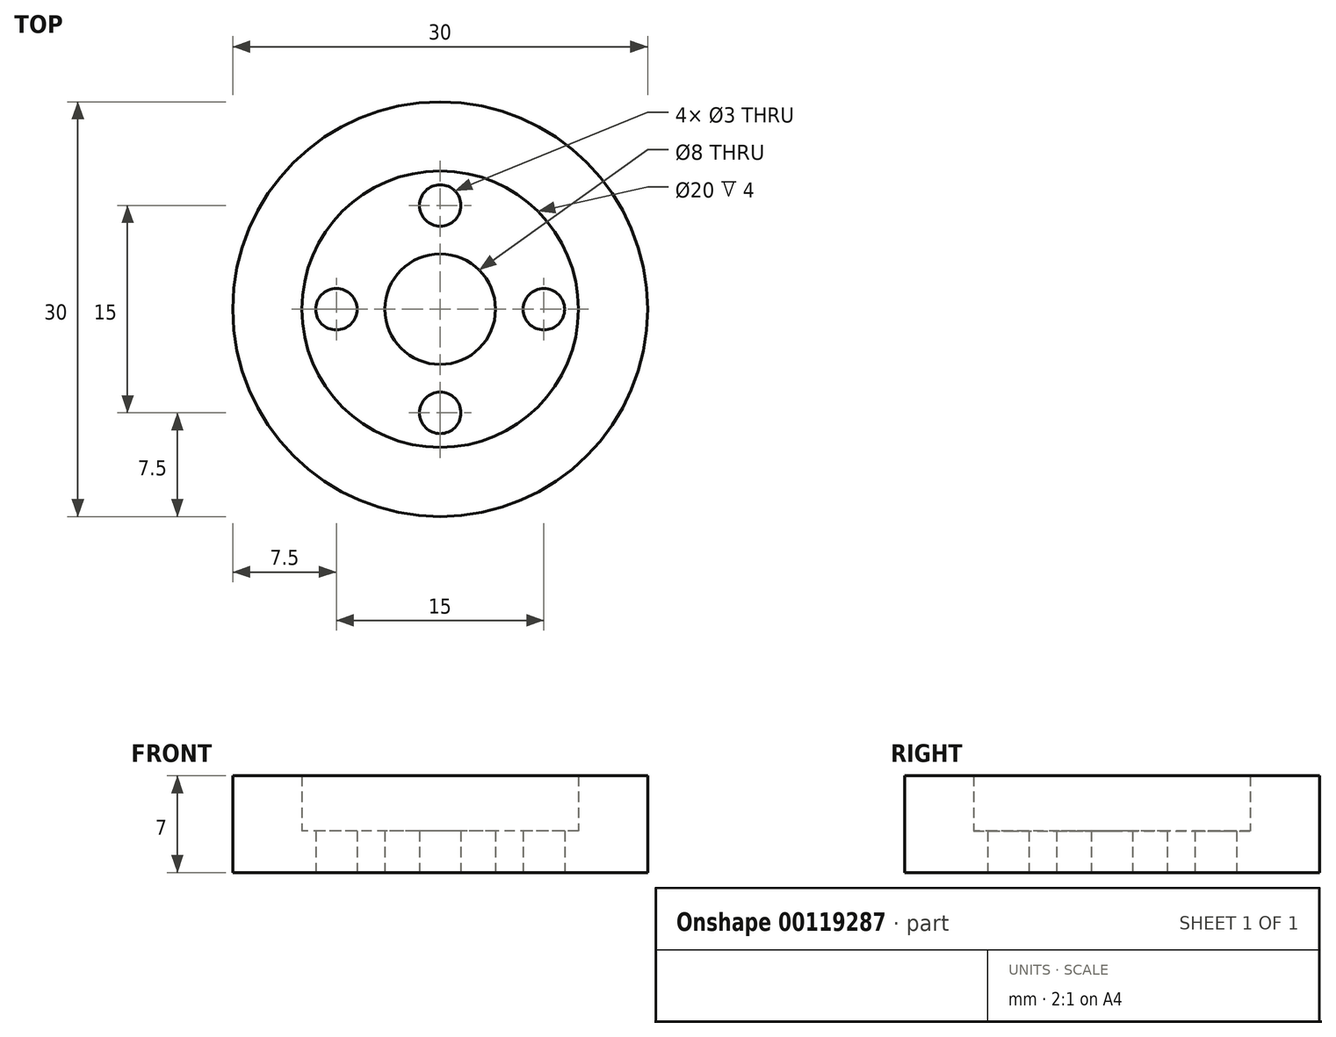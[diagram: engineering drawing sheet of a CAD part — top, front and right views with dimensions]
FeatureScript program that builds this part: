
annotation { "Feature Type Name" : "Feature", "Feature Type Description" : "" }
export const myFeature = defineFeature(function(context is Context, id is Id, definition is map)
    precondition{}
    {
        {
            var Q0;
            Q0=qCreatedBy(makeId("Top.planeOp"),FACE);
            var sketch = newSketch(context, id + "F0", { "sketchPlane" : qUnion([Q0])});
            skCircle(sketch, "E0", {"center": v(0, 0) * mm, "radius": 15 * mm});
            skLineSegment(sketch, "E1", {"start": v(0, 0) * mm, "end": v(0, 7.5) * mm});
            skCircle(sketch, "E2", {"center": v(0, 7.5) * mm, "radius": 1.5 * mm});
            skCircle(sketch, "E3.1.0", {"center": v(-7.5, 0) * mm, "radius": 1.5 * mm});
            skCircle(sketch, "E3.2.0", {"center": v(0, -7.5) * mm, "radius": 1.5 * mm});
            skCircle(sketch, "E3.3.0", {"center": v(7.5, 0) * mm, "radius": 1.5 * mm});
            skCircle(sketch, "E4", {"center": v(0, 0) * mm, "radius": 4 * mm});
            skSolve(sketch);
        }
        {
            var Q0;
            Q0 = qSketchRegion(id + "F0", true);
            extrude(context, id + "F1", {"entities" : qUnion([Q0]), "depth" : 3 * mm});
        }
        {
            var Q0;
            Q0=makeQuery(id+"F1.opExtrude","CAP_FACE",FACE,{"disambiguationData":[OSD([sQuery(id+"F0.wireOp",EDGE,"E0"),sQuery(id+"F0.wireOp",EDGE,"E2"),sQuery(id+"F0.wireOp",EDGE,"E3.1.0"),sQuery(id+"F0.wireOp",EDGE,"E3.2.0"),sQuery(id+"F0.wireOp",EDGE,"E3.3.0"),sQuery(id+"F0.wireOp",EDGE,"E4")])],"isStart":false});
            var sketch = newSketch(context, id + "F2", { "sketchPlane" : qUnion([Q0])});
            skCircle(sketch, "E5.0", {"center": v(0, 0) * mm, "radius": 15 * mm});
            skCircle(sketch, "E6", {"center": v(0, 0) * mm, "radius": 10 * mm});
            skSolve(sketch);
        }
        {
            var Q0;
            Q0 = qSketchRegion(id + "F2", true);
            extrude(context, id + "F3", {"entities" : qUnion([Q0]), "operationType" : NewBodyOperationType.ADD, "depth" : 4 * mm});
        }
    });
